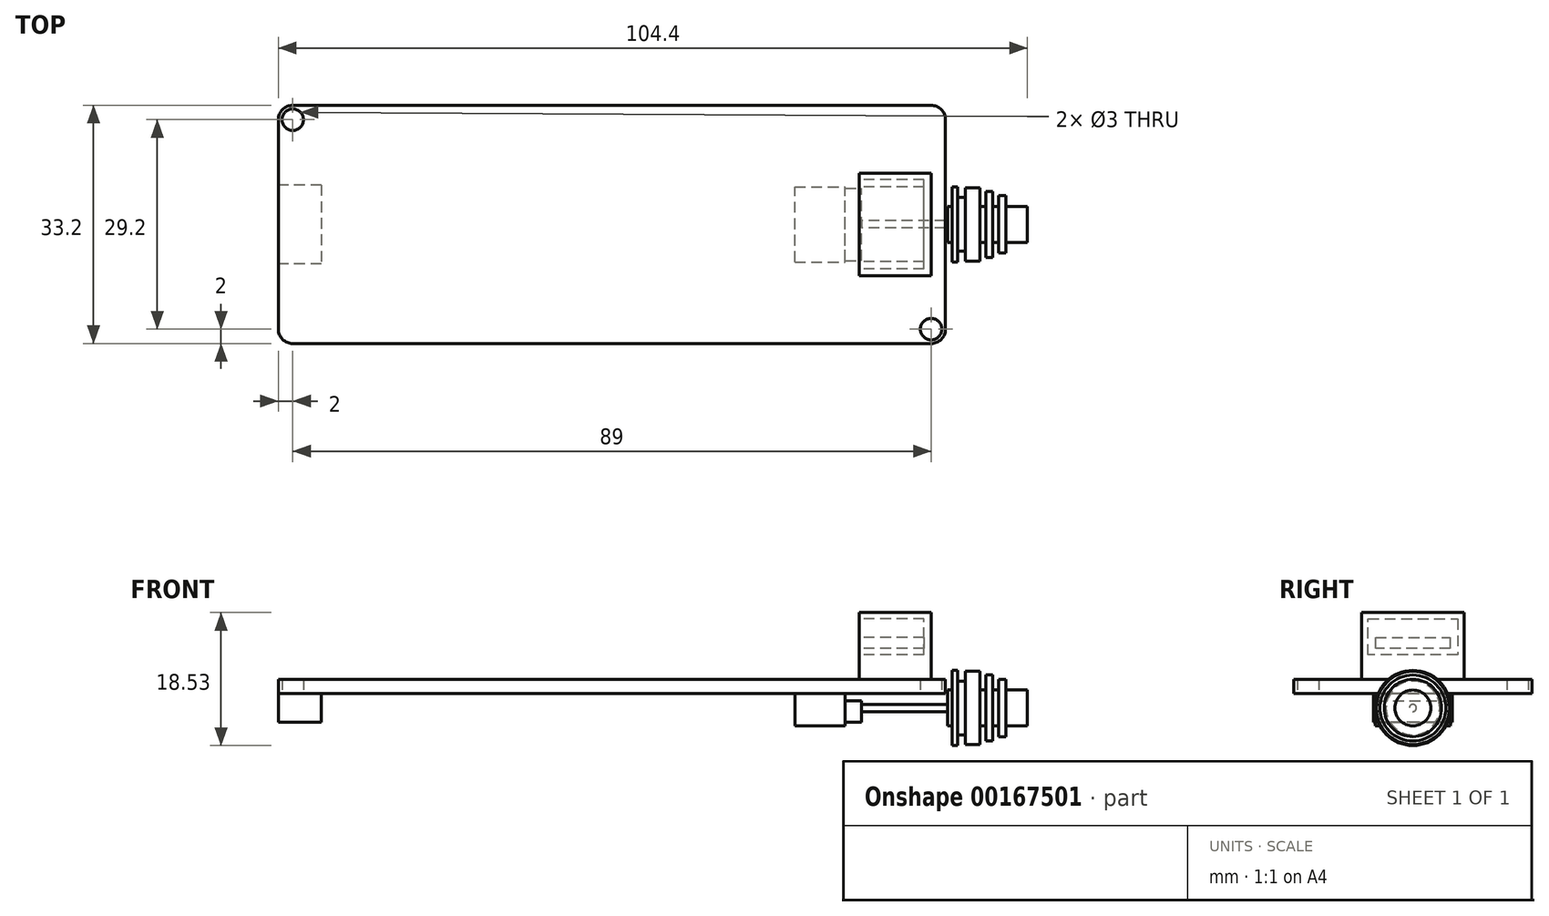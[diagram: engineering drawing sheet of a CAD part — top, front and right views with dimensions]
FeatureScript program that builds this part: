
annotation { "Feature Type Name" : "Feature", "Feature Type Description" : "" }
export const myFeature = defineFeature(function(context is Context, id is Id, definition is map)
    precondition{}
    {
        {
            var Q0;
            Q0=qCreatedBy(makeId("Top.planeOp"),FACE);
            var sketch = newSketch(context, id + "F0", { "sketchPlane" : qUnion([Q0])});
            skLineSegment(sketch, "E0.bottom", {"start": v(2, 0) * mm, "end": v(91, 0) * mm});
            skLineSegment(sketch, "E0.top", {"start": v(2, -33.2) * mm, "end": v(91, -33.2) * mm});
            skLineSegment(sketch, "E0.left", {"start": v(0, -2) * mm, "end": v(0, -31.2) * mm});
            skLineSegment(sketch, "E0.right", {"start": v(93, -2) * mm, "end": v(93, -31.2) * mm});
            skPoint(sketch, "E1.visualSharp", {"position": v(93, 0) * mm});
            skArc(sketch, "E1.filletArc", {"start": v(93, -2) * mm, "mid": v(92.41, -0.59) * mm, "end": v(91, 0) * mm});
            skPoint(sketch, "E2.visualSharp", {"position": v(93, -33.2) * mm});
            skArc(sketch, "E2.filletArc", {"start": v(91, -33.2) * mm, "mid": v(92.41, -32.61) * mm, "end": v(93, -31.2) * mm});
            skPoint(sketch, "E3.visualSharp", {"position": v(0, -33.2) * mm});
            skArc(sketch, "E3.filletArc", {"start": v(0, -31.2) * mm, "mid": v(0.59, -32.61) * mm, "end": v(2, -33.2) * mm});
            skPoint(sketch, "E4.visualSharp", {"position": v(0, 0) * mm});
            skArc(sketch, "E4.filletArc", {"start": v(2, 0) * mm, "mid": v(0.59, -0.59) * mm, "end": v(0, -2) * mm});
            skCircle(sketch, "E5", {"center": v(2, -2) * mm, "radius": 1.5 * mm});
            skCircle(sketch, "E6", {"center": v(91, -31.2) * mm, "radius": 1.5 * mm});
            skLineSegment(sketch, "E7", {"start": v(0, -16.6) * mm, "end": v(93, -16.6) * mm, "construction": true});
            skLineSegment(sketch, "E8", {"start": v(46.5, 0) * mm, "end": v(46.5, -33.2) * mm, "construction": true});
            skSolve(sketch);
        }
        {
            var Q0;
            Q0=makeQuery(id+"F0.imprint","IMPRINT",FACE,{"disambiguationData":[TD([[makeQuery(id+"F0.imprint","IMPRINT",EDGE,{"derivedFrom":sQuery(id+"F0.wireOp",EDGE,"E0.bottom")}),-1.0]])]});
            extrude(context, id + "F1", {"entities" : qUnion([Q0]), "depth" : 2 * mm});
        }
        {
            var Q0;
            Q0=makeQuery(id+"F1.opExtrude","CAP_FACE",FACE,{"disambiguationData":[OSD([sQuery(id+"F0.wireOp",EDGE,"E0.bottom"),sQuery(id+"F0.wireOp",EDGE,"E0.top"),sQuery(id+"F0.wireOp",EDGE,"E0.left"),sQuery(id+"F0.wireOp",EDGE,"E0.right"),sQuery(id+"F0.wireOp",EDGE,"E1.filletArc"),sQuery(id+"F0.wireOp",EDGE,"E2.filletArc"),sQuery(id+"F0.wireOp",EDGE,"E3.filletArc"),sQuery(id+"F0.wireOp",EDGE,"E4.filletArc"),sQuery(id+"F0.wireOp",EDGE,"E5"),sQuery(id+"F0.wireOp",EDGE,"E6")])],"isStart":false});
            var sketch = newSketch(context, id + "F2", { "sketchPlane" : qUnion([Q0])});
            skLineSegment(sketch, "E9.bottom", {"start": v(81, -9.45) * mm, "end": v(91, -9.45) * mm});
            skLineSegment(sketch, "E9.top", {"start": v(81, -23.75) * mm, "end": v(91, -23.75) * mm});
            skLineSegment(sketch, "E9.left", {"start": v(81, -9.45) * mm, "end": v(81, -23.75) * mm});
            skLineSegment(sketch, "E9.right", {"start": v(91, -9.45) * mm, "end": v(91, -23.75) * mm});
            skPoint(sketch, "E10", {"position": v(91, -16.6) * mm});
            skSolve(sketch);
        }
        {
            var Q0;
            Q0=makeQuery(id+"F2.imprint","IMPRINT",FACE,{"disambiguationData":[TD([[makeQuery(id+"F2.imprint","IMPRINT",EDGE,{"derivedFrom":sQuery(id+"F2.wireOp",EDGE,"E9.bottom")}),-1.0]])]});
            extrude(context, id + "F3", {"entities" : qUnion([Q0]), "depth" : 9.3 * mm});
        }
        {
            var Q0;
            Q0=makeQuery(id+"F3.opExtrude","SWEPT_FACE",FACE,{"disambiguationData":[OSD([sQuery(id+"F2.wireOp",EDGE,"E9.left")])]});
            var sketch = newSketch(context, id + "F4", { "sketchPlane" : qUnion([Q0])});
            skLineSegment(sketch, "E11.0.0", {"start": v(11.4, 7.8) * mm, "end": v(11.4, 6.3) * mm});
            skLineSegment(sketch, "E12.0.0", {"start": v(22.83, 10.4) * mm, "end": v(10.38, 10.4) * mm});
            skLineSegment(sketch, "E12.0.1", {"start": v(10.38, 10.4) * mm, "end": v(10.38, 5.4) * mm});
            skLineSegment(sketch, "E12.0.2", {"start": v(10.38, 5.4) * mm, "end": v(22.83, 5.4) * mm});
            skLineSegment(sketch, "E12.0.3", {"start": v(22.83, 5.4) * mm, "end": v(22.83, 10.4) * mm});
            skLineSegment(sketch, "E11.0.1", {"start": v(11.4, 6.3) * mm, "end": v(21.8, 6.3) * mm});
            skLineSegment(sketch, "E11.0.2", {"start": v(21.8, 6.3) * mm, "end": v(21.8, 7.8) * mm});
            skLineSegment(sketch, "E11.0.3", {"start": v(21.8, 7.8) * mm, "end": v(11.4, 7.8) * mm});
            skLineSegment(sketch, "E13.0", {"start": v(9.45, 11.3) * mm, "end": v(23.75, 11.3) * mm, "construction": true});
            skLineSegment(sketch, "E14.0", {"start": v(9.45, 11.3) * mm, "end": v(9.45, 2) * mm, "construction": true});
            skLineSegment(sketch, "E15.0", {"start": v(23.75, 11.3) * mm, "end": v(23.75, 2) * mm, "construction": true});
            skLineSegment(sketch, "E16.0", {"start": v(9.45, 2) * mm, "end": v(23.75, 2) * mm, "construction": true});
            skSolve(sketch);
        }
        {
            var Q0;
            Q0=makeQuery(id+"F4.imprint","IMPRINT",FACE,{"disambiguationData":[TD([[makeQuery(id+"F4.imprint","IMPRINT",EDGE,{"derivedFrom":sQuery(id+"F4.wireOp",EDGE,"E11.0.0")}),-1.0]])]});
            extrude(context, id + "F5", {"entities" : qUnion([Q0]), "operationType" : NewBodyOperationType.REMOVE, "oppositeDirection" : true, "depth" : 9 * mm});
        }
        {
            var Q0;
            Q0=makeQuery(id+"F1.opExtrude","CAP_FACE",FACE,{"disambiguationData":[OSD([sQuery(id+"F0.wireOp",EDGE,"E0.bottom"),sQuery(id+"F0.wireOp",EDGE,"E0.top"),sQuery(id+"F0.wireOp",EDGE,"E0.left"),sQuery(id+"F0.wireOp",EDGE,"E0.right"),sQuery(id+"F0.wireOp",EDGE,"E1.filletArc"),sQuery(id+"F0.wireOp",EDGE,"E2.filletArc"),sQuery(id+"F0.wireOp",EDGE,"E3.filletArc"),sQuery(id+"F0.wireOp",EDGE,"E4.filletArc"),sQuery(id+"F0.wireOp",EDGE,"E5"),sQuery(id+"F0.wireOp",EDGE,"E6")])],"isStart":true});
            var sketch = newSketch(context, id + "F6", { "sketchPlane" : qUnion([Q0])});
            skLineSegment(sketch, "E17.bottom", {"start": v(72, 21.85) * mm, "end": v(79, 21.85) * mm});
            skLineSegment(sketch, "E17.top", {"start": v(72, 11.35) * mm, "end": v(79, 11.35) * mm});
            skLineSegment(sketch, "E17.left", {"start": v(72, 21.85) * mm, "end": v(72, 11.35) * mm});
            skLineSegment(sketch, "E17.right", {"start": v(79, 21.85) * mm, "end": v(79, 11.35) * mm});
            skPoint(sketch, "E18", {"position": v(79, 16.6) * mm});
            skLineSegment(sketch, "E19.bottom", {"start": v(79, 21.65) * mm, "end": v(81.3, 21.65) * mm});
            skLineSegment(sketch, "E19.top", {"start": v(79, 11.55) * mm, "end": v(81.3, 11.55) * mm});
            skLineSegment(sketch, "E19.left", {"start": v(79, 21.65) * mm, "end": v(79, 11.55) * mm});
            skLineSegment(sketch, "E19.right", {"start": v(81.3, 21.65) * mm, "end": v(81.3, 11.55) * mm});
            skLineSegment(sketch, "E20", {"start": v(79, 16.6) * mm, "end": v(100.65, 16.6) * mm, "construction": true});
            skLineSegment(sketch, "E21", {"start": v(93.3, 17.1) * mm, "end": v(93.3, 19.1) * mm});
            skLineSegment(sketch, "E22", {"start": v(93.3, 19.1) * mm, "end": v(93.9, 19.1) * mm});
            skLineSegment(sketch, "E23", {"start": v(93.9, 19.1) * mm, "end": v(93.9, 21.82) * mm});
            skLineSegment(sketch, "E24", {"start": v(93.9, 21.82) * mm, "end": v(94.7, 21.82) * mm});
            skLineSegment(sketch, "E25", {"start": v(94.7, 21.82) * mm, "end": v(94.7, 20.35) * mm});
            skLineSegment(sketch, "E26", {"start": v(94.7, 20.35) * mm, "end": v(95.8, 20.35) * mm});
            skLineSegment(sketch, "E27", {"start": v(95.8, 20.35) * mm, "end": v(95.8, 21.7) * mm});
            skLineSegment(sketch, "E28", {"start": v(95.8, 21.7) * mm, "end": v(97.8, 21.7) * mm});
            skLineSegment(sketch, "E29", {"start": v(97.8, 21.7) * mm, "end": v(97.8, 19.1) * mm});
            skLineSegment(sketch, "E30", {"start": v(97.8, 19.1) * mm, "end": v(98.6, 19.1) * mm});
            skLineSegment(sketch, "E31", {"start": v(98.6, 19.1) * mm, "end": v(98.6, 21.2) * mm});
            skLineSegment(sketch, "E32", {"start": v(98.6, 21.2) * mm, "end": v(99.6, 21.2) * mm});
            skLineSegment(sketch, "E33", {"start": v(99.6, 21.2) * mm, "end": v(99.6, 19.1) * mm});
            skLineSegment(sketch, "E34", {"start": v(99.6, 19.1) * mm, "end": v(100.4, 19.1) * mm});
            skLineSegment(sketch, "E35", {"start": v(100.4, 19.1) * mm, "end": v(100.4, 20.6) * mm});
            skLineSegment(sketch, "E36", {"start": v(100.4, 20.6) * mm, "end": v(101.4, 20.6) * mm});
            skLineSegment(sketch, "E37", {"start": v(101.4, 20.6) * mm, "end": v(101.4, 19.1) * mm});
            skLineSegment(sketch, "E38", {"start": v(101.4, 19.1) * mm, "end": v(104.4, 19.1) * mm});
            skLineSegment(sketch, "E39", {"start": v(104.4, 19.1) * mm, "end": v(104.4, 16.6) * mm});
            skLineSegment(sketch, "E40", {"start": v(93.3, 17.1) * mm, "end": v(81.3, 17.1) * mm});
            skLineSegment(sketch, "E41.bottom", {"start": v(6, 11.1) * mm, "end": v(0, 11.1) * mm});
            skLineSegment(sketch, "E41.top", {"start": v(6, 22.1) * mm, "end": v(0, 22.1) * mm});
            skLineSegment(sketch, "E41.left", {"start": v(6, 11.1) * mm, "end": v(6, 22.1) * mm});
            skLineSegment(sketch, "E41.right", {"start": v(0, 11.1) * mm, "end": v(0, 22.1) * mm});
            skPoint(sketch, "E42", {"position": v(6, 16.6) * mm});
            skLineSegment(sketch, "E43", {"start": v(104.4, 16.6) * mm, "end": v(81.3, 16.6) * mm});
            skSolve(sketch);
        }
        {
            var Q0;
            Q0=makeQuery(id+"F6.imprint","IMPRINT",FACE,{"disambiguationData":[TD([[makeQuery(id+"F6.imprint","IMPRINT",EDGE,{"derivedFrom":sQuery(id+"F6.wireOp",EDGE,"E17.bottom")}),-1.0]])]});
            extrude(context, id + "F7", {"entities" : qUnion([Q0]), "depth" : 4.5 * mm});
        }
        {
            var Q0;
            {var subQ5=sQuery(id+"F6.wireOp",EDGE,"E19.right");Q0=makeQuery(id+"F6.imprint","IMPRINT",FACE,{"disambiguationData":[TD([[makeQuery(id+"F6.imprint","IMPRINT",EDGE,{"derivedFrom":subQ5}),-1.0]])]});}
            var Q1;
            {var subQ0=sQuery(id+"F6.wireOp",EDGE,"E19.left");Q1=makeQuery(id+"F6.imprint","IMPRINT",FACE,{"disambiguationData":[TD([[makeQuery(id+"F6.imprint","IMPRINT",EDGE,{"derivedFrom":subQ0}),1.0]])]});}
            extrude(context, id + "F8", {"entities" : qUnion([Q0, Q1]), "depth" : 4 * mm, "hasSecondDirection" : true, "secondDirectionOppositeDirection" : false, "secondDirectionDepth" : 1 * mm});
        }
        {
            var Q0;
            Q0=makeQuery(id+"F6.imprint","IMPRINT",FACE,{"disambiguationData":[TD([[makeQuery(id+"F6.imprint","IMPRINT",EDGE,{"derivedFrom":sQuery(id+"F6.wireOp",EDGE,"E21")}),-1.0]])]});
            var Q1;
            {var subQ3=sQuery(id+"F6.wireOp",EDGE,"E19.right");var subQ5=sQuery(id+"F6.wireOp",EDGE,"E40");var subQ7=makeQuery(id+"F6.imprint","INTERSECT",VERTEX,{"derivedFrom":[subQ3,subQ5]});Q1=makeQuery(id+"F6.imprint","IMPRINT",FACE,{"disambiguationData":[TD([[makeQuery(id+"F6.imprint","IMPRINT",EDGE,{"disambiguationData":[TD([[subQ7,-1.0]])],"derivedFrom":subQ3}),1.0]])]});}
            var Q2;
            Q2=sQuery(id+"F6.wireOp",EDGE,"E20");
            revolve(context, id + "F9", {"entities" : qUnion([Q0, Q1]), "axis" : qUnion([Q2]), "revolveType" : RevolveType.FULL});
        }
        {
            var Q0;
            Q0=makeQuery(id+"F9.opRevolve","SWEPT_BODY",BODY,{"disambiguationData":[OSD([sQuery(id+"F6.wireOp",EDGE,"E21"),sQuery(id+"F6.wireOp",EDGE,"E22"),sQuery(id+"F6.wireOp",EDGE,"E23"),sQuery(id+"F6.wireOp",EDGE,"E24"),sQuery(id+"F6.wireOp",EDGE,"E25"),sQuery(id+"F6.wireOp",EDGE,"E26"),sQuery(id+"F6.wireOp",EDGE,"E27"),sQuery(id+"F6.wireOp",EDGE,"E28"),sQuery(id+"F6.wireOp",EDGE,"E29"),sQuery(id+"F6.wireOp",EDGE,"E30"),sQuery(id+"F6.wireOp",EDGE,"E31"),sQuery(id+"F6.wireOp",EDGE,"E32"),sQuery(id+"F6.wireOp",EDGE,"E33"),sQuery(id+"F6.wireOp",EDGE,"E34"),sQuery(id+"F6.wireOp",EDGE,"E35"),sQuery(id+"F6.wireOp",EDGE,"E36"),sQuery(id+"F6.wireOp",EDGE,"E37"),sQuery(id+"F6.wireOp",EDGE,"E38"),sQuery(id+"F6.wireOp",EDGE,"E39"),sQuery(id+"F6.wireOp",EDGE,"fea964b9-c608-4439-ae80-985564ab3df6")])]});
            transform(context, id + "F10", {"entities" : qUnion([Q0]), "transformType" : TransformType.TRANSLATION_3D, "dx" : 0 * mm, "dy" : 0 * mm, "dz" : -2 * mm, "makeCopy" : false});
        }
        {
            var Q0;
            Q0=makeQuery(id+"F6.imprint","IMPRINT",FACE,{"disambiguationData":[TD([[makeQuery(id+"F6.imprint","IMPRINT",EDGE,{"derivedFrom":sQuery(id+"F6.wireOp",EDGE,"E41.bottom")}),-1.0]])]});
            extrude(context, id + "F11", {"entities" : qUnion([Q0]), "depth" : 4 * mm});
        }
    });
